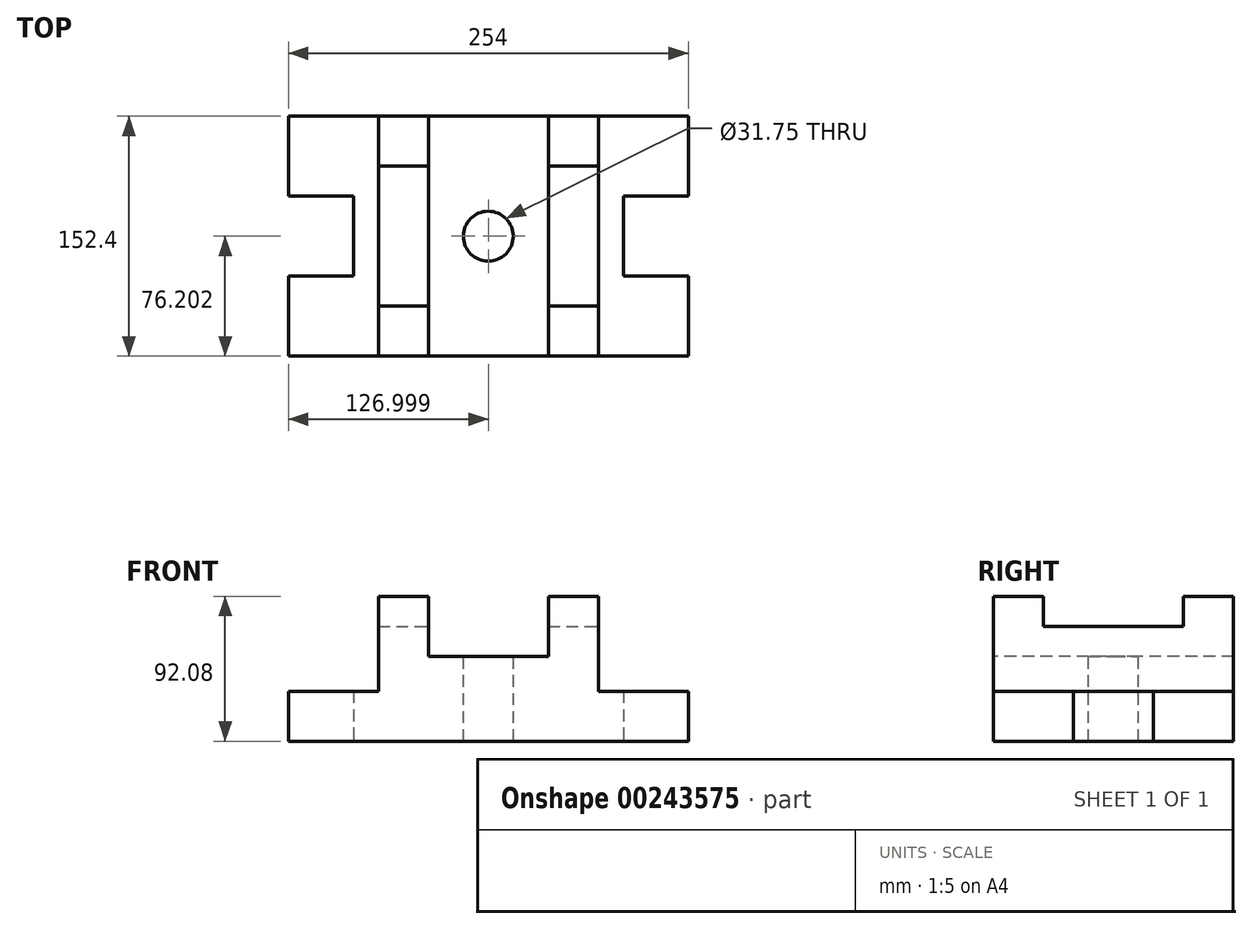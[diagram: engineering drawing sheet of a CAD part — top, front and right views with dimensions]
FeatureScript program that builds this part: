
annotation { "Feature Type Name" : "Feature", "Feature Type Description" : "" }
export const myFeature = defineFeature(function(context is Context, id is Id, definition is map)
    precondition{}
    {
        {
            var Q0;
            Q0=qCreatedBy(makeId("Top.planeOp"),FACE);
            var sketch = newSketch(context, id + "F0", { "sketchPlane" : qUnion([Q0])});
            skLineSegment(sketch, "E0", {"start": v(-14.3, 73.1) * mm, "end": v(239.7, 73.1) * mm});
            skLineSegment(sketch, "E1", {"start": v(239.7, 73.1) * mm, "end": v(239.7, 22.3) * mm});
            skLineSegment(sketch, "E2", {"start": v(239.7, 22.3) * mm, "end": v(198.43, 22.3) * mm});
            skLineSegment(sketch, "E3", {"start": v(198.43, 22.3) * mm, "end": v(198.43, -28.5) * mm});
            skLineSegment(sketch, "E4", {"start": v(198.43, -28.5) * mm, "end": v(239.7, -28.5) * mm});
            skLineSegment(sketch, "E5", {"start": v(239.7, -28.5) * mm, "end": v(239.7, -79.3) * mm});
            skLineSegment(sketch, "E6", {"start": v(239.7, -79.3) * mm, "end": v(-14.3, -79.3) * mm});
            skLineSegment(sketch, "E7", {"start": v(-14.3, 73.1) * mm, "end": v(-14.3, 22.3) * mm});
            skLineSegment(sketch, "E8", {"start": v(-14.3, 22.3) * mm, "end": v(26.98, 22.3) * mm});
            skLineSegment(sketch, "E9", {"start": v(26.98, 22.3) * mm, "end": v(26.98, -28.5) * mm});
            skLineSegment(sketch, "E10", {"start": v(26.98, -28.5) * mm, "end": v(-14.3, -28.5) * mm});
            skLineSegment(sketch, "E11", {"start": v(-14.3, -28.5) * mm, "end": v(-14.3, -79.3) * mm});
            skSolve(sketch);
        }
        {
            var Q0;
            Q0=makeQuery(id+"F0.imprint","IMPRINT",FACE,{"disambiguationData":[TD([[makeQuery(id+"F0.imprint","IMPRINT",EDGE,{"derivedFrom":sQuery(id+"F0.wireOp",EDGE,"E0")}),-1.0]])]});
            extrude(context, id + "F1", {"entities" : qUnion([Q0]), "depth" : 31.75 * mm});
        }
        {
            var Q0;
            Q0=makeQuery(id+"F1.opExtrude","CAP_FACE",FACE,{"disambiguationData":[OSD([sQuery(id+"F0.wireOp",EDGE,"E0"),sQuery(id+"F0.wireOp",EDGE,"E1"),sQuery(id+"F0.wireOp",EDGE,"E2"),sQuery(id+"F0.wireOp",EDGE,"E3"),sQuery(id+"F0.wireOp",EDGE,"E4"),sQuery(id+"F0.wireOp",EDGE,"E5"),sQuery(id+"F0.wireOp",EDGE,"E6"),sQuery(id+"F0.wireOp",EDGE,"E7"),sQuery(id+"F0.wireOp",EDGE,"E8"),sQuery(id+"F0.wireOp",EDGE,"E9"),sQuery(id+"F0.wireOp",EDGE,"E10"),sQuery(id+"F0.wireOp",EDGE,"E11")])],"isStart":false});
            var sketch = newSketch(context, id + "F2", { "sketchPlane" : qUnion([Q0])});
            skLineSegment(sketch, "E12.bottom", {"start": v(42.86, 73.1) * mm, "end": v(182.56, 73.1) * mm});
            skLineSegment(sketch, "E12.top", {"start": v(42.86, -79.3) * mm, "end": v(182.56, -79.3) * mm});
            skLineSegment(sketch, "E12.left", {"start": v(42.86, 73.1) * mm, "end": v(42.86, -79.3) * mm});
            skLineSegment(sketch, "E12.right", {"start": v(182.56, 73.1) * mm, "end": v(182.56, -79.3) * mm});
            skPoint(sketch, "E13.startSnap0", {"position": v(182.56, -3.1) * mm});
            skSolve(sketch);
        }
        {
            var Q0;
            Q0=makeQuery(id+"F2.imprint","IMPRINT",FACE,{"disambiguationData":[TD([[makeQuery(id+"F2.imprint","IMPRINT",EDGE,{"derivedFrom":sQuery(id+"F2.wireOp",EDGE,"E12.bottom")}),-1.0]])]});
            extrude(context, id + "F3", {"entities" : qUnion([Q0]), "operationType" : NewBodyOperationType.ADD, "depth" : 22.22 * mm});
        }
        {
            var Q0;
            Q0=makeQuery(id+"F3.opExtrude","CAP_FACE",FACE,{"disambiguationData":[OSD([sQuery(id+"F2.wireOp",EDGE,"E12.bottom"),sQuery(id+"F2.wireOp",EDGE,"E12.top"),sQuery(id+"F2.wireOp",EDGE,"E12.left"),sQuery(id+"F2.wireOp",EDGE,"E12.right")])],"isStart":false});
            var sketch = newSketch(context, id + "F4", { "sketchPlane" : qUnion([Q0])});
            skLineSegment(sketch, "E14", {"start": v(74.6, 73.1) * mm, "end": v(74.6, -79.3) * mm});
            skLineSegment(sketch, "E15", {"start": v(150.8, 73.1) * mm, "end": v(150.8, -79.3) * mm});
            skSolve(sketch);
        }
        {
            var Q0;
            {var subQ0=sQuery(id+"F4.wireOp",EDGE,"E14");Q0=makeQuery(id+"F4.imprint","IMPRINT",FACE,{"disambiguationData":[TD([[makeQuery(id+"F4.imprint","IMPRINT",EDGE,{"derivedFrom":subQ0}),-1.0]])]});}
            var Q1;
            {var subQ0=sQuery(id+"F4.wireOp",EDGE,"E15");Q1=makeQuery(id+"F4.imprint","IMPRINT",FACE,{"disambiguationData":[TD([[makeQuery(id+"F4.imprint","IMPRINT",EDGE,{"derivedFrom":subQ0}),1.0]])]});}
            extrude(context, id + "F5", {"entities" : qUnion([Q0, Q1]), "operationType" : NewBodyOperationType.ADD, "depth" : 19.05 * mm});
        }
        {
            var Q0;
            Q0=makeQuery(id+"F5.opExtrude","CAP_FACE",FACE,{"disambiguationData":[OSD([sQuery(id+"F2.wireOp",EDGE,"E12.bottom"),sQuery(id+"F2.wireOp",EDGE,"E12.top"),sQuery(id+"F2.wireOp",EDGE,"E12.left"),sQuery(id+"F4.wireOp",EDGE,"E14")])],"isStart":false});
            var sketch = newSketch(context, id + "F6", { "sketchPlane" : qUnion([Q0])});
            skLineSegment(sketch, "E16", {"start": v(42.86, 41.34) * mm, "end": v(74.6, 41.34) * mm});
            skLineSegment(sketch, "E17", {"start": v(42.86, -47.56) * mm, "end": v(74.6, -47.56) * mm});
            skSolve(sketch);
        }
        {
            var Q0;
            {var subQ0=sQuery(id+"F6.wireOp",EDGE,"E16");Q0=makeQuery(id+"F6.imprint","IMPRINT",FACE,{"disambiguationData":[TD([[makeQuery(id+"F6.imprint","IMPRINT",EDGE,{"derivedFrom":subQ0}),1.0]])]});}
            var Q1;
            {var subQ0=sQuery(id+"F6.wireOp",EDGE,"E17");Q1=makeQuery(id+"F6.imprint","IMPRINT",FACE,{"disambiguationData":[TD([[makeQuery(id+"F6.imprint","IMPRINT",EDGE,{"derivedFrom":subQ0}),-1.0]])]});}
            extrude(context, id + "F7", {"entities" : qUnion([Q0, Q1]), "operationType" : NewBodyOperationType.ADD, "depth" : 19.05 * mm});
        }
        {
            var Q0;
            Q0=makeQuery(id+"F5.opExtrude","CAP_FACE",FACE,{"disambiguationData":[OSD([sQuery(id+"F2.wireOp",EDGE,"E12.bottom"),sQuery(id+"F2.wireOp",EDGE,"E12.top"),sQuery(id+"F2.wireOp",EDGE,"E12.right"),sQuery(id+"F4.wireOp",EDGE,"E15")])],"isStart":false});
            var sketch = newSketch(context, id + "F8", { "sketchPlane" : qUnion([Q0])});
            skLineSegment(sketch, "E18", {"start": v(150.8, 41.34) * mm, "end": v(182.56, 41.34) * mm});
            skLineSegment(sketch, "E19", {"start": v(150.8, -3.1) * mm, "end": v(182.56, -3.1) * mm});
            skLineSegment(sketch, "E20", {"start": v(150.8, -47.56) * mm, "end": v(182.56, -47.56) * mm});
            skSolve(sketch);
        }
        {
            var Q0;
            {var subQ0=sQuery(id+"F8.wireOp",EDGE,"E18");Q0=makeQuery(id+"F8.imprint","IMPRINT",FACE,{"disambiguationData":[TD([[makeQuery(id+"F8.imprint","IMPRINT",EDGE,{"derivedFrom":subQ0}),1.0]])]});}
            var Q1;
            {var subQ0=sQuery(id+"F8.wireOp",EDGE,"E20");Q1=makeQuery(id+"F8.imprint","IMPRINT",FACE,{"disambiguationData":[TD([[makeQuery(id+"F8.imprint","IMPRINT",EDGE,{"derivedFrom":subQ0}),-1.0]])]});}
            extrude(context, id + "F9", {"entities" : qUnion([Q0, Q1]), "operationType" : NewBodyOperationType.ADD, "depth" : 19.05 * mm});
        }
        {
            var Q0;
            Q0=makeQuery(id+"F3.opExtrude","CAP_FACE",FACE,{"disambiguationData":[OSD([sQuery(id+"F2.wireOp",EDGE,"E12.bottom"),sQuery(id+"F2.wireOp",EDGE,"E12.top"),sQuery(id+"F2.wireOp",EDGE,"E12.left"),sQuery(id+"F2.wireOp",EDGE,"E12.right")])],"isStart":false});
            var sketch = newSketch(context, id + "F10", { "sketchPlane" : qUnion([Q0])});
            skLineSegment(sketch, "E21", {"start": v(112.7, -79.3) * mm, "end": v(112.7, -3.1) * mm});
            skCircle(sketch, "E22", {"center": v(112.7, -3.1) * mm, "radius": 15.88 * mm});
            skSolve(sketch);
        }
        {
            var Q0;
            Q0=makeQuery(id+"F10.imprint","IMPRINT",FACE,{"disambiguationData":[TD([[makeQuery(id+"F10.imprint","IMPRINT",EDGE,{"derivedFrom":sQuery(id+"F10.wireOp",EDGE,"E22")}),1.0]])]});
            extrude(context, id + "F11", {"entities" : qUnion([Q0]), "operationType" : NewBodyOperationType.REMOVE, "endBound" : BoundingType.THROUGH_ALL, "oppositeDirection" : true, "depth" : 25.4 * mm});
        }
    });
